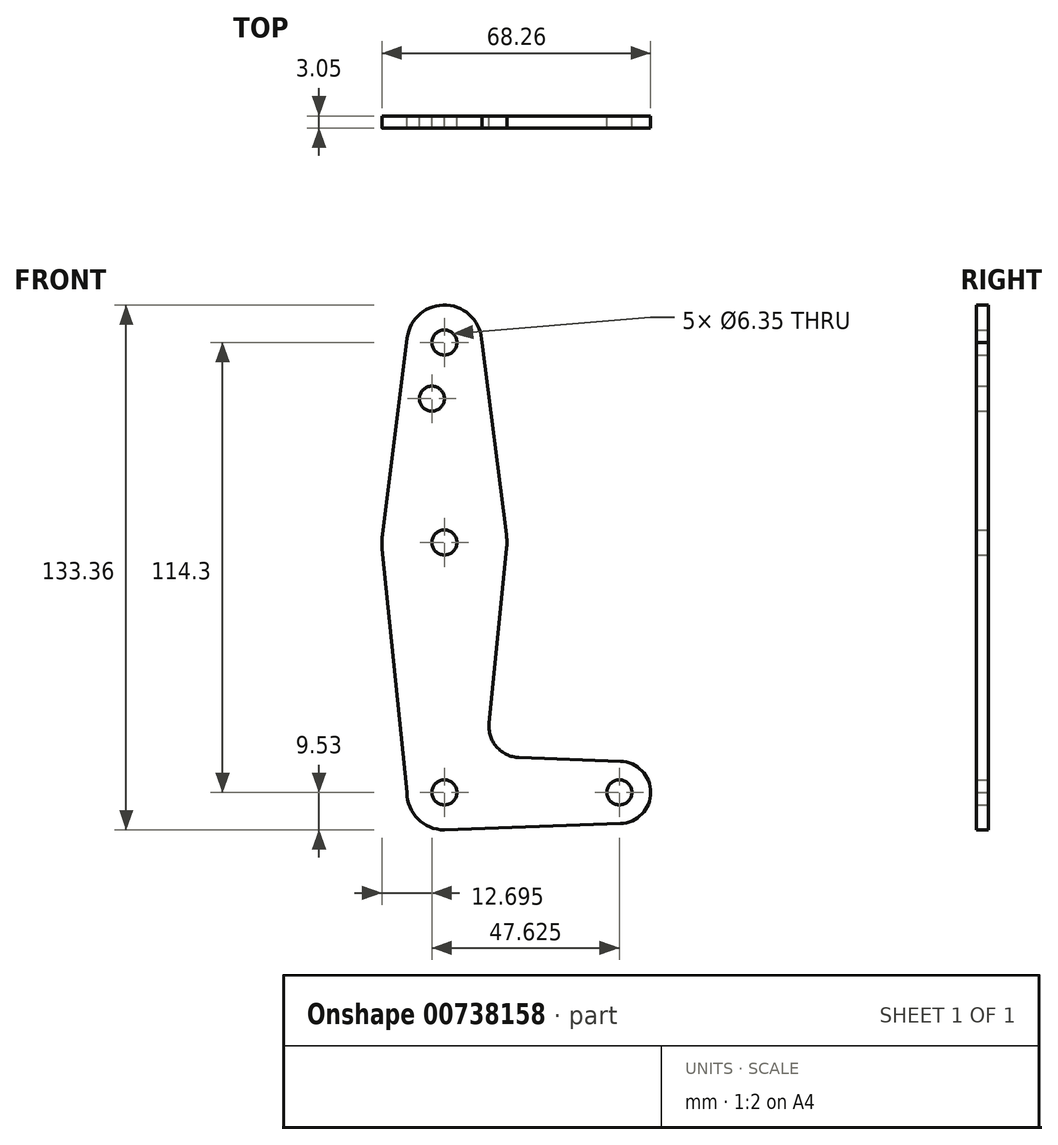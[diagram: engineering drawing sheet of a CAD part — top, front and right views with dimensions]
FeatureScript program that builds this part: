
annotation { "Feature Type Name" : "Feature", "Feature Type Description" : "" }
export const myFeature = defineFeature(function(context is Context, id is Id, definition is map)
    precondition{}
    {
        {
            var Q0;
            Q0=qCreatedBy(makeId("Front.planeOp"),FACE);
            var sketch = newSketch(context, id + "F0", { "sketchPlane" : qUnion([Q0])});
            skLineSegment(sketch, "E0", {"start": v(0, 63.5) * mm, "end": v(0, 114.3) * mm, "construction": true});
            skLineSegment(sketch, "E1", {"start": v(0, 0) * mm, "end": v(44.45, 0) * mm, "construction": true});
            skCircle(sketch, "E2", {"center": v(0, 0) * mm, "radius": 9.53 * mm});
            skCircle(sketch, "E3", {"center": v(0, 63.5) * mm, "radius": 15.88 * mm});
            skCircle(sketch, "E4", {"center": v(0, 114.3) * mm, "radius": 9.53 * mm});
            skCircle(sketch, "E5", {"center": v(44.45, 0) * mm, "radius": 7.94 * mm});
            skLineSegment(sketch, "E6", {"start": v(-9.45, 115.5) * mm, "end": v(-15.75, 65.48) * mm});
            skLineSegment(sketch, "E7", {"start": v(9.53, 114.3) * mm, "end": v(15.75, 65.5) * mm});
            skCircle(sketch, "E8", {"center": v(0, 114.3) * mm, "radius": 3.18 * mm});
            skCircle(sketch, "E9", {"center": v(-3.17, 100.03) * mm, "radius": 3.18 * mm});
            skCircle(sketch, "E10", {"center": v(0, 63.5) * mm, "radius": 3.18 * mm});
            skCircle(sketch, "E11", {"center": v(0, 0) * mm, "radius": 3.18 * mm});
            skCircle(sketch, "E12", {"center": v(44.45, 0) * mm, "radius": 3.18 * mm});
            skLineSegment(sketch, "E13", {"start": v(0, -9.53) * mm, "end": v(44.73, -7.93) * mm});
            skLineSegment(sketch, "E14", {"start": v(15.8, 61.91) * mm, "end": v(11.34, 17.6) * mm});
            skLineSegment(sketch, "E15", {"start": v(18.97, 8.85) * mm, "end": v(44.73, 7.93) * mm});
            skLineSegment(sketch, "E16", {"start": v(-15.8, 61.9) * mm, "end": v(-9.52, 0) * mm});
            skArc(sketch, "E17.filletArc", {"start": v(11.34, 17.6) * mm, "mid": v(13.26, 11.57) * mm, "end": v(18.97, 8.85) * mm});
            skLineSegment(sketch, "E18", {"start": v(0, 63.5) * mm, "end": v(0, 0) * mm, "construction": true});
            skSolve(sketch);
        }
        {
            var Q0;
            Q0=makeQuery(id+"F0.imprint","IMPRINT",FACE,{"disambiguationData":[TD([[makeQuery(id+"F0.imprint","IMPRINT",EDGE,{"derivedFrom":sQuery(id+"F0.wireOp",EDGE,"E8")}),-1.0]])]});
            var Q1;
            {var subQ1=sQuery(id+"F0.wireOp",EDGE,"E6");Q1=makeQuery(id+"F0.imprint","IMPRINT",FACE,{"disambiguationData":[TD([[makeQuery(id+"F0.imprint","IMPRINT",EDGE,{"derivedFrom":subQ1}),1.0]])]});}
            var Q2;
            Q2=makeQuery(id+"F0.imprint","IMPRINT",FACE,{"disambiguationData":[TD([[makeQuery(id+"F0.imprint","IMPRINT",EDGE,{"derivedFrom":sQuery(id+"F0.wireOp",EDGE,"E10")}),-1.0]])]});
            var Q3;
            {var subQ6=sQuery(id+"F0.wireOp",EDGE,"E14");Q3=makeQuery(id+"F0.imprint","IMPRINT",FACE,{"disambiguationData":[TD([[makeQuery(id+"F0.imprint","IMPRINT",EDGE,{"derivedFrom":subQ6}),-1.0]])]});}
            var Q4;
            Q4=makeQuery(id+"F0.imprint","IMPRINT",FACE,{"disambiguationData":[TD([[makeQuery(id+"F0.imprint","IMPRINT",EDGE,{"derivedFrom":sQuery(id+"F0.wireOp",EDGE,"E11")}),-1.0]])]});
            var Q5;
            Q5=makeQuery(id+"F0.imprint","IMPRINT",FACE,{"disambiguationData":[TD([[makeQuery(id+"F0.imprint","IMPRINT",EDGE,{"derivedFrom":sQuery(id+"F0.wireOp",EDGE,"E12")}),-1.0]])]});
            extrude(context, id + "F1", {"entities" : qUnion([Q0, Q1, Q2, Q3, Q4, Q5]), "depth" : 3.05 * mm, "offsetDistance" : 25.4 * mm});
        }
    });
